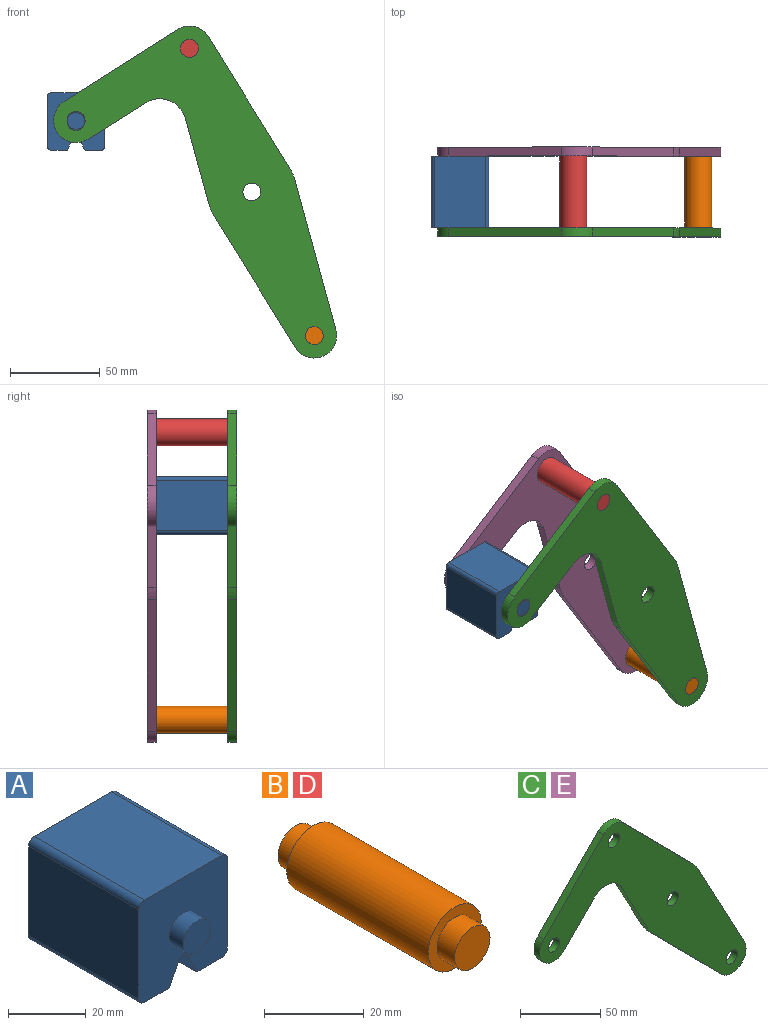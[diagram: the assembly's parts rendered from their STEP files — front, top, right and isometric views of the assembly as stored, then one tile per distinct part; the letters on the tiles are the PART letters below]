
ASSEMBLY  parts=5 mates=3
PART A: 18 faces, bbox 32.1x50x32.1 mm
  f0: plane 40x28.08mm, normal (1,0,0), area 1123.1mm2, adj f4,f10,f13,f14
  f1: plane 40x9.04mm, normal (0,0,-1), area 361.6mm2, adj f2,f4,f10,f14
  f2: plane 40x6.42mm, normal (-0.89,0,-0.45), area 287.2mm2, adj f1,f4,f10,f15
  f3: plane 40x6.42mm, normal (0.89,0,-0.45), area 287.2mm2, adj f4,f5,f10,f15
  f4: plane 32.08x32.08mm, normal (0,-1,0), area 900.6mm2, adj f0,f1,f2,f3,f5,f6,f7,f9
  f5: plane 40x9.04mm, normal (0,0,-1), area 361.6mm2, adj f3,f4,f10,f16
  f6: plane 40x28.08mm, normal (0,0,1), area 1123.1mm2, adj f4,f10,f13,f17
  f7: plane 40x28.08mm, normal (-1,0,0), area 1123.1mm2, adj f4,f10,f16,f17
  f8: plane 10x10mm, normal (0,-1,0), area 78.5mm2, adj f9
  f9: cylinder r=5mm len=10mm, axis (0,1,0), area 157.1mm2, adj f4,f8
  f10: plane 32.08x32.08mm, normal (0,1,0), area 900.6mm2, adj f0,f1,f2,f3,f5,f6,f7,f12
  f11: plane 10x10mm, normal (0,1,0), area 78.5mm2, adj f12
  f12: cylinder r=5mm len=10mm, axis (0,-1,0), area 157.1mm2, adj f10,f11
  f13: cylinder r=2mm len=40mm, axis (0,1,0), area 125.7mm2, adj f0,f4,f6,f10
  f14: cylinder r=2mm len=40mm, axis (0,-1,0), area 125.7mm2, adj f0,f1,f4,f10
  f15: cylinder r=2mm len=40mm, axis (0,1,0), area 177.1mm2, adj f2,f3,f4,f10
  f16: cylinder r=2mm len=40mm, axis (0,1,0), area 125.7mm2, adj f4,f5,f7,f10
  f17: cylinder r=2mm len=40mm, axis (0,-1,0), area 125.7mm2, adj f4,f6,f7,f10
PART B: 7 faces, bbox 15x50x15 mm
  f0: cylinder r=7.5mm len=40mm, axis (0,-1,0), area 1885mm2, adj f2,f5
  f1: cylinder r=5mm len=10mm, axis (0,1,0), area 157.1mm2, adj f2,f3
  f2: plane 15x15mm, normal (0,-1,0), area 98.2mm2, adj f0,f1
  f3: plane 10x10mm, normal (0,-1,0), area 78.5mm2, adj f1
  f4: cylinder r=5mm len=10mm, axis (0,-1,0), area 157.1mm2, adj f5,f6
  f5: plane 15x15mm, normal (0,1,0), area 98.2mm2, adj f0,f4
  f6: plane 10x10mm, normal (0,1,0), area 78.5mm2, adj f4
PART C: 18 faces, bbox 181.7x5x165.8 mm
  f0: plane 43.49x23.35mm, normal (-0.88,0,-0.47), area 246.8mm2, adj f1,f14,f16,f17
  f1: cylinder r=25mm len=5.75mm, axis (0,1,0), area 35.8mm2, adj f0,f2,f16,f17
  f2: plane 61.6x60.87mm, normal (-0.71,0,-0.7), area 433mm2, adj f1,f3,f16,f17
  f3: cylinder r=12.5mm len=21.39mm, axis (0,1,0), area 178.4mm2, adj f2,f4,f16,f17
  f4: plane 76.3x40.96mm, normal (0.88,0,0.47), area 433mm2, adj f3,f5,f16,f17
  f5: cylinder r=25mm len=5.75mm, axis (0,1,0), area 35.8mm2, adj f4,f6,f16,f17
  f6: plane 61.6x60.87mm, normal (0.71,0,0.7), area 433mm2, adj f5,f7,f16,f17
  f7: cylinder r=12.5mm len=17.78mm, axis (0,1,0), area 98.9mm2, adj f6,f8,f16,f17
  f8: plane 53.35x52.71mm, normal (-0.71,0,0.7), area 375mm2, adj f7,f9,f16,f17
  f9: cylinder r=12.5mm len=21.39mm, axis (0,1,0), area 196.3mm2, adj f8,f10,f16,f17
  f10: plane 26.86x26.54mm, normal (0.71,0,-0.7), area 188.8mm2, adj f9,f14,f16,f17
  f11: cylinder r=5mm len=10mm, axis (0,1,0), area 157.1mm2, adj f16,f17
  f12: cylinder r=5mm len=10mm, axis (0,1,0), area 157.1mm2, adj f16,f17
  f13: cylinder r=5mm len=10mm, axis (0,1,0), area 157.1mm2, adj f16,f17
  f14: cylinder r=15mm len=23.89mm, axis (0,1,0), area 140.2mm2, adj f0,f10,f16,f17
  f15: cylinder r=5mm len=10mm, axis (0,1,0), area 157.1mm2, adj f16,f17
  f16: plane 181.66x165.78mm, normal (0,-1,0), area 8710.1mm2, adj f0,f1,f2,f3,f4,f5,f6,f7
  f17: plane 181.66x165.78mm, normal (0,1,0), area 8710.1mm2, adj f0,f1,f2,f3,f4,f5,f6,f7
PART D: same geometry as B
PART E: same geometry as C
PLACE A t=(6.48,-20,22.35)mm
PLACE B rot(axis=(0,1,0),12.9deg) t=(69.76,-20,-160.49)mm
PLACE C rot(axis=(0,1,0),12.9deg) t=(0,-20,0)mm fixed
PLACE D rot(axis=(0,1,0),12.9deg) t=(0,-20,0)mm
PLACE E rot(axis=(0,1,0),12.9deg) t=(0,25,0)mm
MATE fastened D.f0 <-> E.f7  axis (0,1,0) through (-34.88,20,80.25)mm
MATE revolute C.f9 <-> A.f4  axis (0,1,0) through (-98.21,-20,40.06)mm
MATE fastened B.f0 <-> C.f3  axis (0,1,0) through (34.88,-20,-80.25)mm
